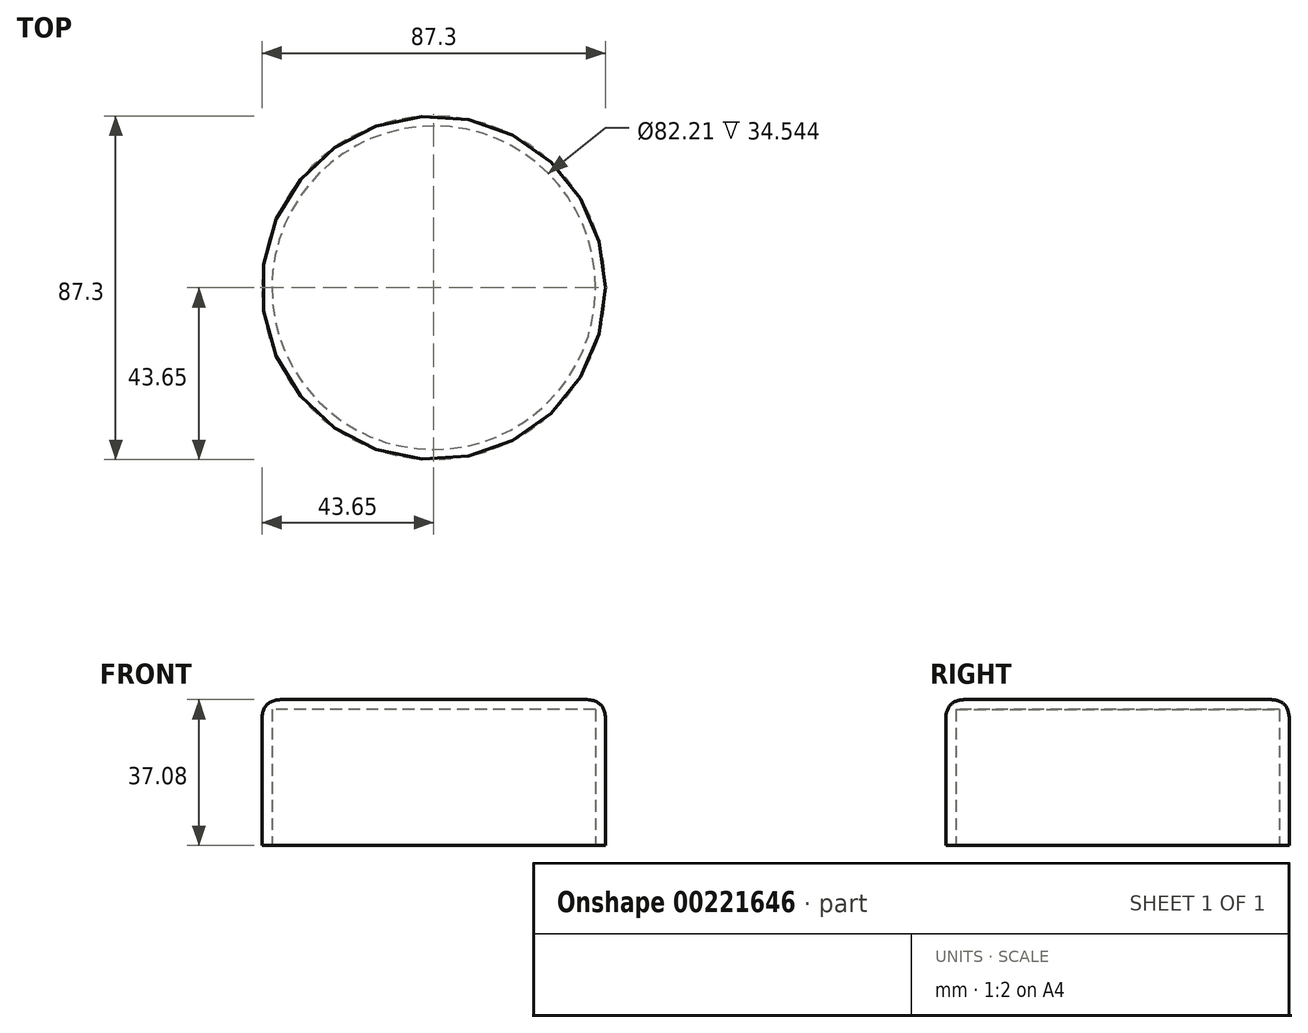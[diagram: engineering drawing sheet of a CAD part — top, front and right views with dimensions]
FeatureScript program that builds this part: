
annotation { "Feature Type Name" : "Feature", "Feature Type Description" : "" }
export const myFeature = defineFeature(function(context is Context, id is Id, definition is map)
    precondition{}
    {
        {
            var Q0;
            Q0=qCreatedBy(makeId("Top.planeOp"),FACE);
            var sketch = newSketch(context, id + "F0", { "sketchPlane" : qUnion([Q0])});
            skCircle(sketch, "E0", {"center": v(0, 0) * mm, "radius": 43.65 * mm});
            skSolve(sketch);
        }
        {
            var Q0;
            Q0 = qSketchRegion(id + "F0", true);
            extrude(context, id + "F1", {"entities" : qUnion([Q0]), "depth" : 37.08 * mm});
        }
        {
            var Q0;
            Q0=makeQuery(id+"F1.opExtrude","CAP_FACE",FACE,{"disambiguationData":[OSD([sQuery(id+"F0.wireOp",EDGE,"E0")])],"isStart":true});
            shell(context, id + "F2", {"entities" : qUnion([Q0]), "thickness" : 2.54 * mm});
        }
        {
            var Q0;
            Q0=makeQuery(id+"F1.opExtrude","CAP_FACE",FACE,{"disambiguationData":[OSD([sQuery(id+"F0.wireOp",EDGE,"E0")])],"isStart":false});
            fillet(context, id + "F3", {"entities" : qUnion([Q0]), "radius" : 5.08 * mm, "tangentPropagation" : true, "rho" : 0.5, "crossSection" : FilletCrossSection.CONIC, "allowEdgeOverflow" : false});
        }
    });
